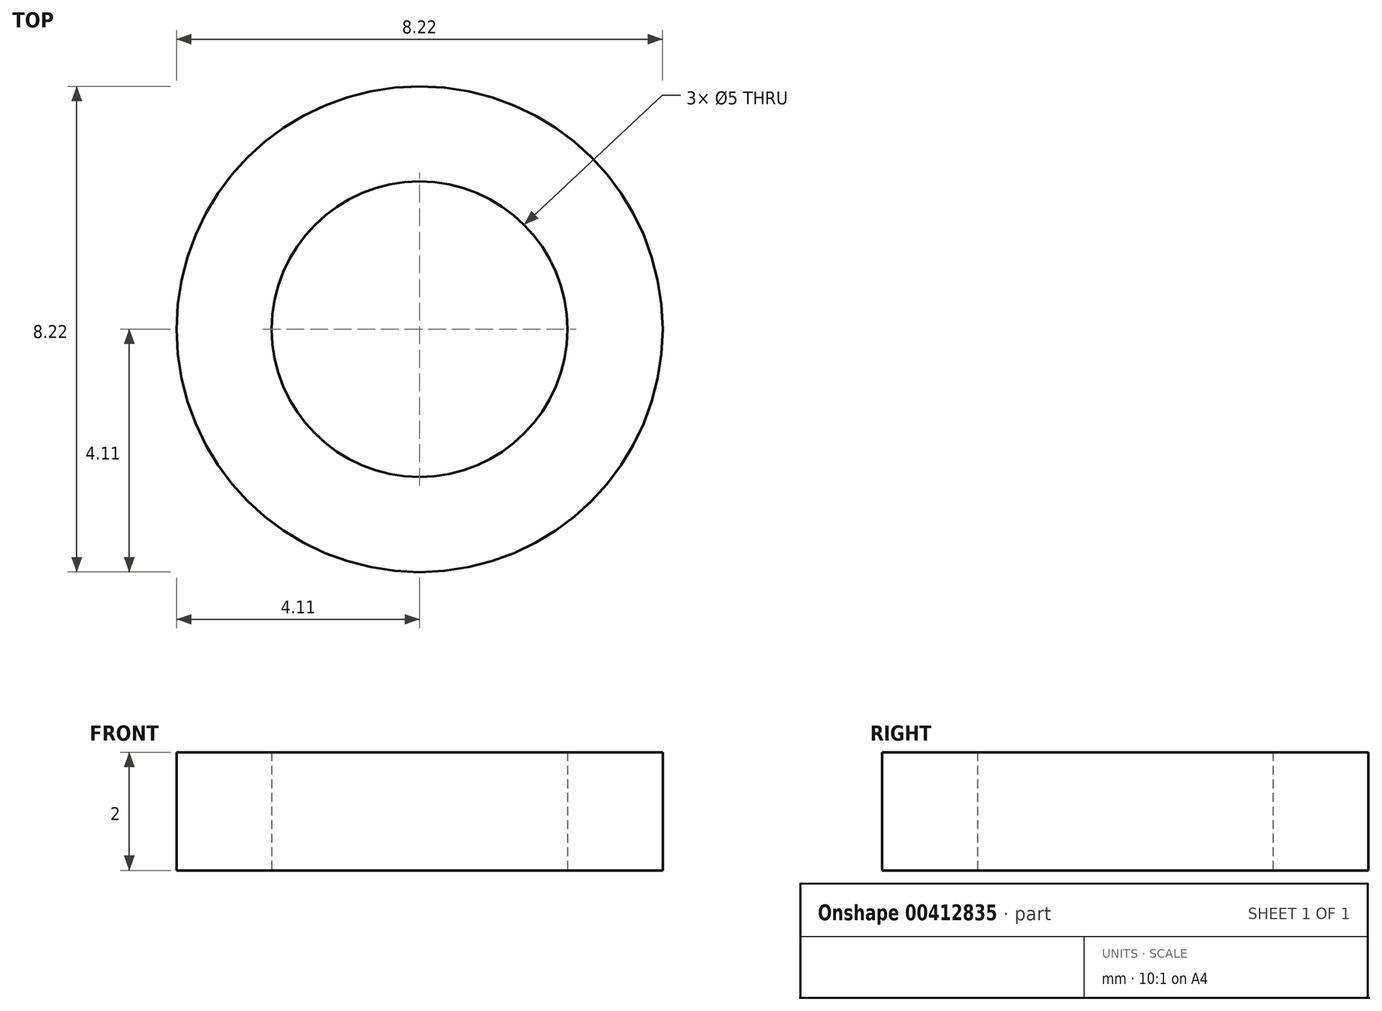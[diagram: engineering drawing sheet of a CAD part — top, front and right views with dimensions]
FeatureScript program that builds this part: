
annotation { "Feature Type Name" : "Feature", "Feature Type Description" : "" }
export const myFeature = defineFeature(function(context is Context, id is Id, definition is map)
    precondition{}
    {
        {
            var Q0;
            Q0=qCreatedBy(makeId("Top.planeOp"),FACE);
            var sketch = newSketch(context, id + "F0", { "sketchPlane" : qUnion([Q0])});
            skCircle(sketch, "E0", {"center": v(-2.5, 0) * mm, "radius": 2.5 * mm});
            skCircle(sketch, "E1", {"center": v(-2.5, 0) * mm, "radius": 4.11 * mm});
            skSolve(sketch);
        }
        {
            var Q0;
            Q0=makeQuery(id+"F0.imprint","IMPRINT",FACE,{"disambiguationData":[TD([[makeQuery(id+"F0.imprint","IMPRINT",EDGE,{"derivedFrom":sQuery(id+"F0.wireOp",EDGE,"E0")}),-1.0]])]});
            extrude(context, id + "F1", {"entities" : qUnion([Q0]), "depth" : 2 * mm});
        }
    });
